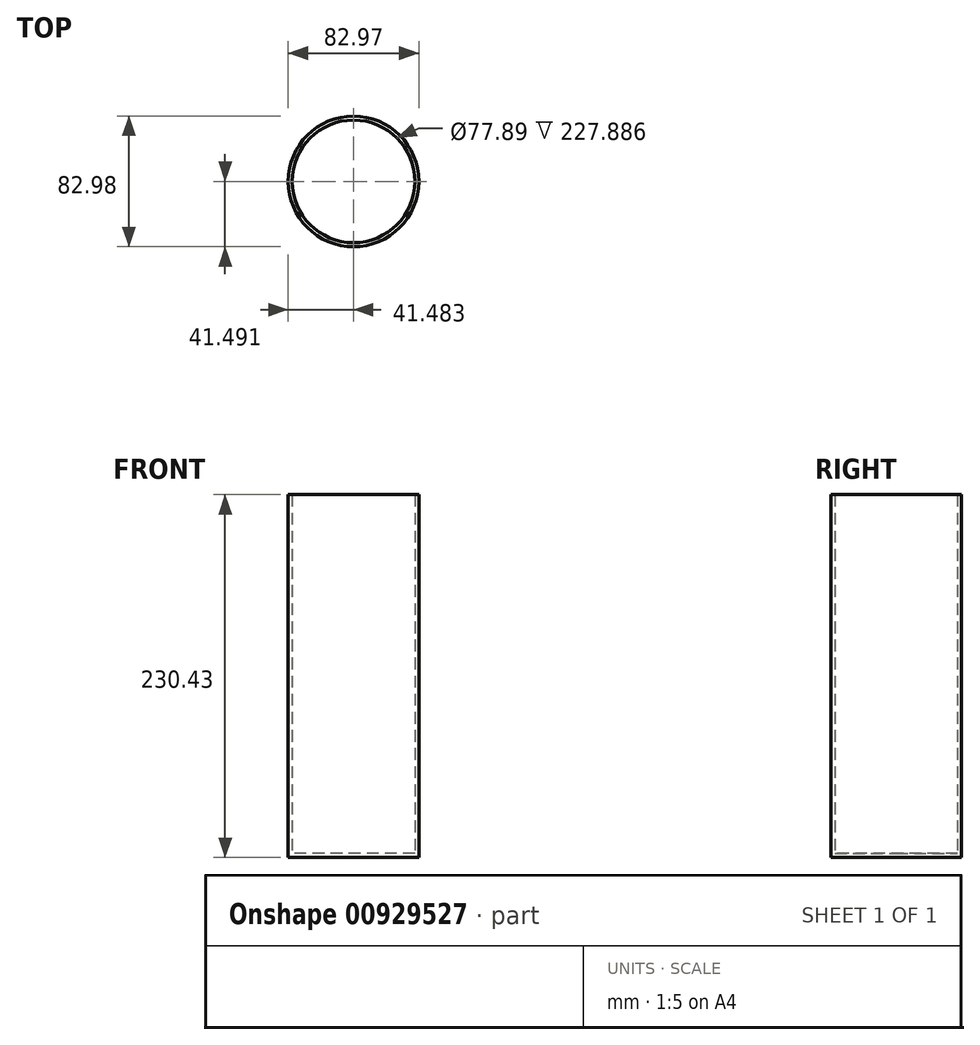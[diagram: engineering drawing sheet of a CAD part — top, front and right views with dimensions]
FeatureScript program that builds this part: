
annotation { "Feature Type Name" : "Feature", "Feature Type Description" : "" }
export const myFeature = defineFeature(function(context is Context, id is Id, definition is map)
    precondition{}
    {
        {
            var Q0;
            Q0=qCreatedBy(makeId("Top.planeOp"),FACE);
            var sketch = newSketch(context, id + "F0", { "sketchPlane" : qUnion([Q0])});
            skCircle(sketch, "E0", {"center": v(3.12, 20.64) * mm, "radius": 41.49 * mm});
            skPoint(sketch, "E0.first.point", {"position": v(0, -20.73) * mm});
            skPoint(sketch, "E0.second.point", {"position": v(39.11, 0) * mm});
            skPoint(sketch, "E0.third.point", {"position": v(31.79, 50.63) * mm});
            skSolve(sketch);
        }
        {
            var Q0;
            Q0=makeQuery(id+"F0.imprint","IMPRINT",FACE,{"disambiguationData":[TD([[makeQuery(id+"F0.imprint","IMPRINT",EDGE,{"derivedFrom":sQuery(id+"F0.wireOp",EDGE,"E0")}),1.0]])]});
            var sketch = newSketch(context, id + "F1", { "sketchPlane" : qUnion([Q0])});
            skSolve(sketch);
        }
        {
            var Q0;
            Q0=makeQuery(id+"F1.imprint","IMPRINT",FACE,{"disambiguationData":[TD([[makeQuery(id+"F1.imprint","IMPRINT",EDGE,{"derivedFrom":makeQuery(id+"F0.imprint","IMPRINT",EDGE,{"derivedFrom":sQuery(id+"F0.wireOp",EDGE,"E0")})}),1.0]])]});
            extrude(context, id + "F2", {"entities" : qUnion([Q0]), "depth" : 230.43 * mm, "offsetDistance" : 25.4 * mm});
        }
        {
            var Q0;
            Q0=makeQuery(id+"F2.opExtrude","CAP_FACE",FACE,{"disambiguationData":[OSD([sQuery(id+"F0.wireOp",EDGE,"E0")])],"isStart":false});
            shell(context, id + "F3", {"entities" : qUnion([Q0]), "thickness" : 2.54 * mm});
        }
    });
